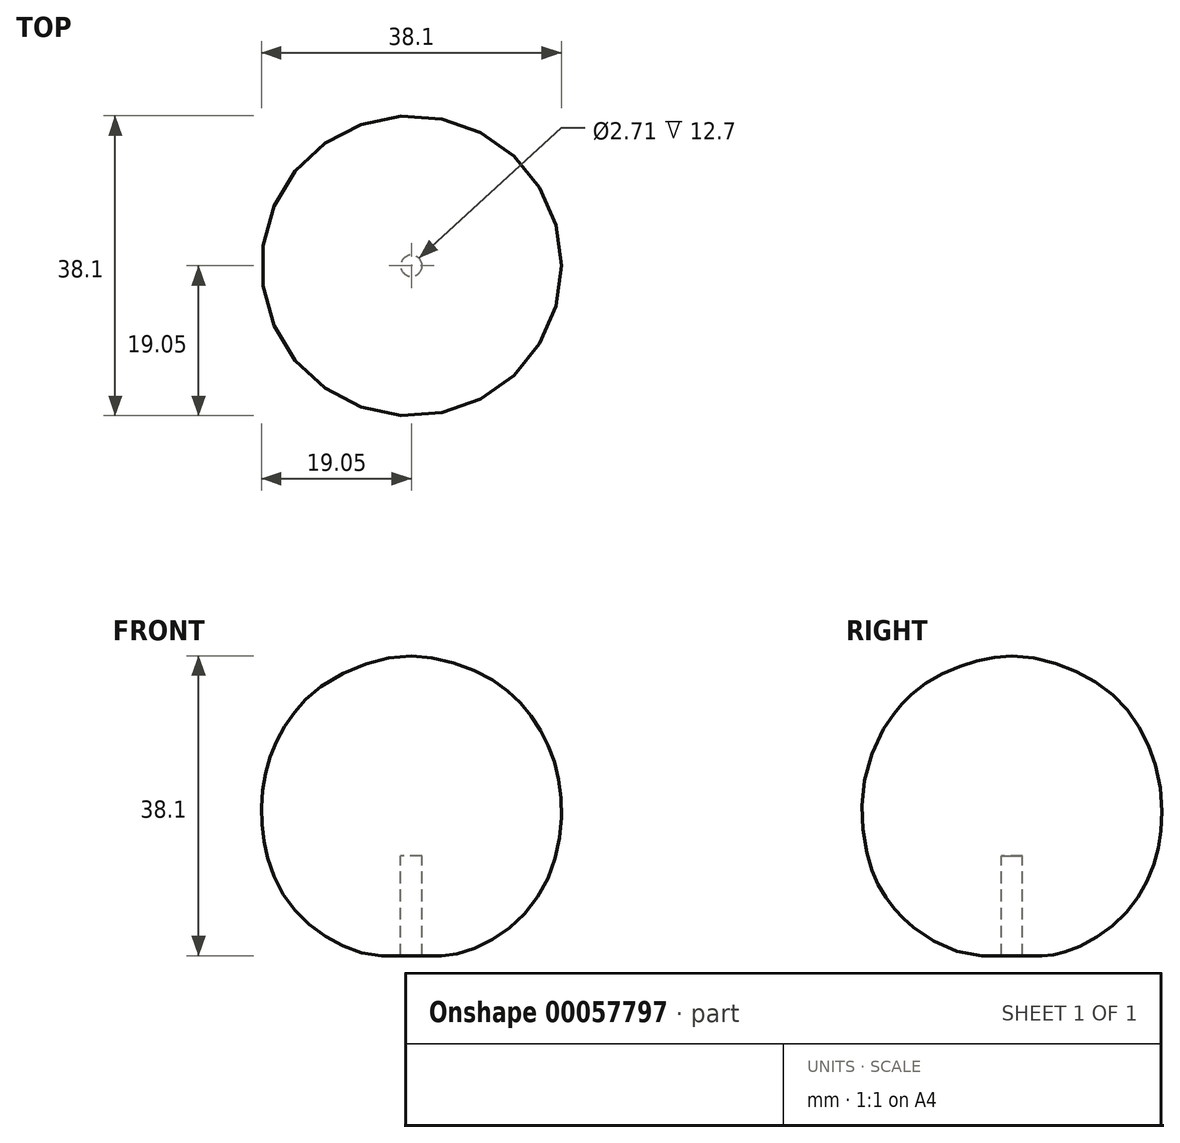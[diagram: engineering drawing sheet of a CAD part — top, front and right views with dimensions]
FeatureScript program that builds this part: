
annotation { "Feature Type Name" : "Feature", "Feature Type Description" : "" }
export const myFeature = defineFeature(function(context is Context, id is Id, definition is map)
    precondition{}
    {
        {
            var Q0;
            Q0=qCreatedBy(makeId("Front.planeOp"),FACE);
            var sketch = newSketch(context, id + "F0", { "sketchPlane" : qUnion([Q0])});
            skLineSegment(sketch, "E0", {"start": v(0, 0) * mm, "end": v(3.81, 0) * mm});
            skFitSpline(sketch, "E1", {"points": [v(3.81, 0) * mm, v(10.45, 2.14) * mm, v(16.89, 8.87) * mm, v(19.05, 18.06) * mm, v(17.9, 25.34) * mm, v(14.87, 30.92) * mm, v(9.53, 35.44) * mm, v(0, 38.1) * mm], "startDerivative": vector(42.7, 0) * mm, "endDerivative": vector(-57.7, 0) * mm});
            skLineSegment(sketch, "E2", {"start": v(1.35, 0) * mm, "end": v(1.35, 12.7) * mm});
            skLineSegment(sketch, "E3", {"start": v(1.35, 12.7) * mm, "end": v(0, 12.7) * mm});
            skLineSegment(sketch, "E4", {"start": v(0, 38.1) * mm, "end": v(0, 12.7) * mm});
            skSolve(sketch);
        }
        {
            var Q0;
            Q0 = qSketchRegion(id + "F0", true);
            var Q1;
            Q1=sQuery(id+"F0.wireOp",EDGE,"E4");
            revolve(context, id + "F1", {"entities" : qUnion([Q0]), "axis" : qUnion([Q1]), "revolveType" : RevolveType.FULL});
        }
    });
